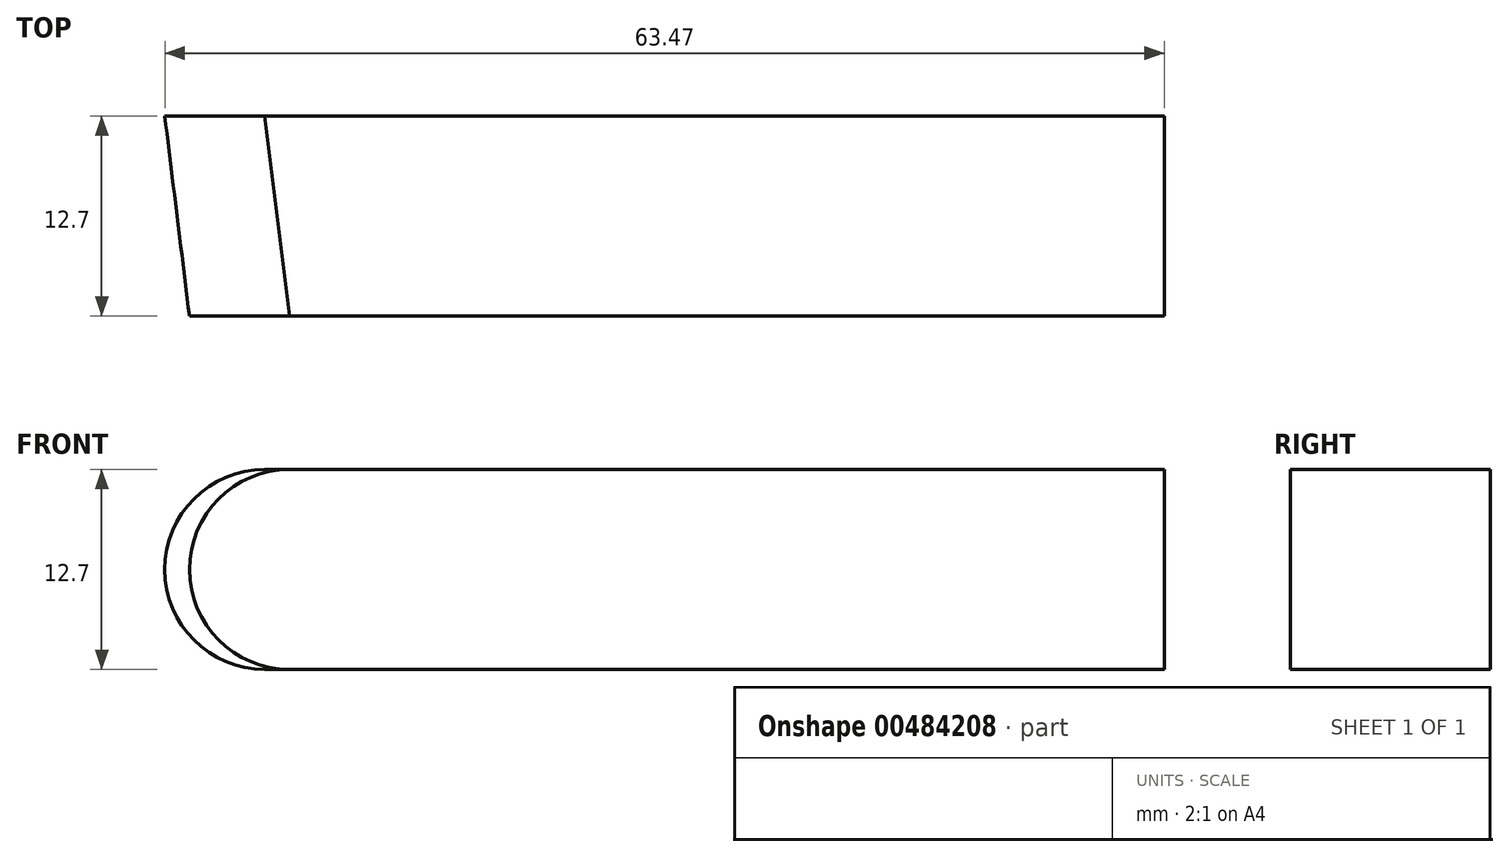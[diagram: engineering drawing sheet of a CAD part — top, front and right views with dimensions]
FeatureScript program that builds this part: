
annotation { "Feature Type Name" : "Feature", "Feature Type Description" : "" }
export const myFeature = defineFeature(function(context is Context, id is Id, definition is map)
    precondition{}
    {
        {
            var Q0;
            Q0=qCreatedBy(makeId("Front.planeOp"),FACE);
            var sketch = newSketch(context, id + "F0", { "sketchPlane" : qUnion([Q0])});
            skLineSegment(sketch, "E0.bottom", {"start": v(0, 0) * mm, "end": v(63.5, 0) * mm});
            skLineSegment(sketch, "E0.top", {"start": v(0, -12.7) * mm, "end": v(63.5, -12.7) * mm});
            skLineSegment(sketch, "E0.left", {"start": v(0, 0) * mm, "end": v(0, -12.7) * mm});
            skLineSegment(sketch, "E0.right", {"start": v(63.5, 0) * mm, "end": v(63.5, -12.7) * mm});
            skSolve(sketch);
        }
        {
            var Q0;
            Q0 = qSketchRegion(id + "F0", true);
            extrude(context, id + "F1", {"entities" : qUnion([Q0]), "oppositeDirection" : true, "depth" : 12.7 * mm});
        }
        {
            var Q0;
            Q0=makeQuery(id+"F1.opExtrude","CAP_FACE",FACE,{"disambiguationData":[OSD([sQuery(id+"F0.wireOp",EDGE,"E0.bottom"),sQuery(id+"F0.wireOp",EDGE,"E0.top"),sQuery(id+"F0.wireOp",EDGE,"E0.left"),sQuery(id+"F0.wireOp",EDGE,"E0.right")])],"isStart":false});
            var sketch = newSketch(context, id + "F2", { "sketchPlane" : qUnion([Q0])});
            skArc(sketch, "E1", {"start": v(-6.38, -12.7) * mm, "mid": v(-0.03, -6.35) * mm, "end": v(-6.38, 0) * mm});
            skPoint(sketch, "E2.orphan", {"position": v(0, 0) * mm});
            skPoint(sketch, "E3.orphan", {"position": v(0, -12.7) * mm});
            skPoint(sketch, "E4.0.end.orphan", {"position": v(-63.5, 0) * mm});
            skPoint(sketch, "E5.0.end.orphan", {"position": v(-63.5, -12.7) * mm});
            skSolve(sketch);
        }
        {
            var Q0;
            Q0=makeQuery(id+"F1.opExtrude","CAP_FACE",FACE,{"disambiguationData":[OSD([sQuery(id+"F0.wireOp",EDGE,"E0.bottom"),sQuery(id+"F0.wireOp",EDGE,"E0.top"),sQuery(id+"F0.wireOp",EDGE,"E0.left"),sQuery(id+"F0.wireOp",EDGE,"E0.right")])],"isStart":true});
            var sketch = newSketch(context, id + "F3", { "sketchPlane" : qUnion([Q0])});
            skArc(sketch, "E6", {"start": v(7.94, 0) * mm, "mid": v(1.59, -6.35) * mm, "end": v(7.94, -12.7) * mm});
            skSolve(sketch);
        }
        {
            var Q1;
            {var subQ0=sQuery(id+"F3.wireOp",EDGE,"E6");Q1=makeQuery(id+"F3.imprint","IMPRINT",FACE,{"disambiguationData":[TD([[makeQuery(id+"F3.imprint","IMPRINT",EDGE,{"derivedFrom":subQ0}),-1.0]])]});}
            var Q2;
            {var subQ0=sQuery(id+"F2.wireOp",EDGE,"E1");Q2=makeQuery(id+"F2.imprint","IMPRINT",FACE,{"disambiguationData":[TD([[makeQuery(id+"F2.imprint","IMPRINT",EDGE,{"derivedFrom":subQ0}),-1.0]])]});}
            loft(context, id + "F4", {"operationType" : NewBodyOperationType.REMOVE, "sheetProfilesArray" : [{ "sheetProfileEntities" : qUnion([Q1]) }, { "sheetProfileEntities" : qUnion([Q2]) }]});
        }
    });
